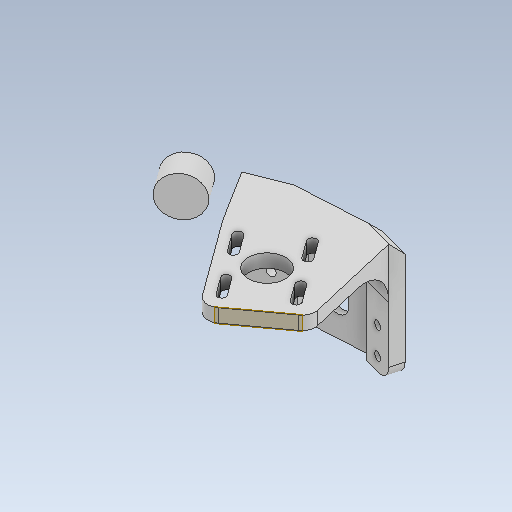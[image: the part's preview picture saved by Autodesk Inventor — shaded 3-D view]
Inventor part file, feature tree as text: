
AUTODESK INVENTOR PART (.ipt)
format: ipt  version: 2020 (Build 240168000, 168)  size: 335,360 bytes
history: native  units: mm
features: reference x10, other x8, sketch x7, extrude x5, fillet x4, projected_geometry x4, plane x2, hole x2, thicken_offset x1, chamfer x1, shell x1
ambient origin geometry x8: Origin, YZ Plane, XZ Plane, XY Plane, X Axis, Y Axis, Z Axis, Center Point
bodies: Solid1 (feature_tree)
feature tree (45):
  plane  "Work Plane1"
  extrude  "Extrusion1"  Depth=5.0mm
  extrude  "Extrusion2"  Depth=5.0mm
  thicken_offset  "Thicken1"
  hole  "Hole1"  [1 undecoded]
  hole  "Hole2"  [1 undecoded]
  extrude  "Extrusion3"  Depth=8.0mm
  fillet  "Fillet1"  Radius=20.0mm
  fillet  "Fillet2"  Radius=20.0mm
  chamfer  "Chamfer1"  Distance=40.0mm
  fillet  "Fillet3"  Radius=4.0mm
  fillet  "Fillet4"  Radius=3.0mm
  extrude  "Extrusion4"  Depth=4.0mm
  plane  "Work Plane2"
  extrude  "Extrusion5"  Depth=10.0mm
  sketch  "Sketch1"  dims[d0=5.0mm d1=5.0mm]
  reference  "Reference1"
  reference  "Reference2"
  reference  "Reference3"
  reference  "Reference4"
  sketch  "Sketch2"  dims[d2=5.0mm d3=5.0mm]
  projected_geometry  "Projected Loop1"
  projected_geometry  "Projected Loop2"
  sketch  "Sketch3"  dims[d4=25.0mm d5=0.0mm d6=25.0mm d7=0.0mm]
  reference  "Reference5"
  reference  "Reference6"
  sketch  "Sketch4"  dims[d8=20.0mm d9=20.0mm]
  reference  "Reference7"
  reference  "Reference8"
  sketch  "Sketch5"  dims[d10=3.0mm d11=6.0mm d12=4.0mm d13=2.0mm d14=90.0deg d15=8.0mm d16=20.594885mm]
  reference  "Reference9"
  projected_geometry  "Projected Loop3"
  sketch  "Sketch6"  dims[d17=3.0mm d18=6.0mm d19=4.0mm d20=2.0mm d21=90.0deg d22=8.0mm d23=20.594885mm d24=102.0mm d25=20.0mm d26=20.0mm]
  projected_geometry  "Projected Loop4"
  sketch  "Sketch7"  dims[d27=30.0mm d28=40.0mm d29=4.0mm d30=3.0mm d31=4.0mm d32=3.2mm d33=4.0mm d34=3.2mm d35=4.0mm d36=3.2mm d37=14.0mm d38=5.0mm d39=0.0mm d40=14.0mm d41=2.0mm d42=5.0mm d43=2.0mm d44=45.0deg d45=5.0mm d46=5.0mm d47=18.0mm d48=6.0mm d49=8.0mm d50=5.0mm d51=0.0mm d52=0.0mm d53=55.0mm d54=15.0mm d55=10.0mm d56=0.0mm]
  reference  "Reference10"
  parser-record x2  (decoder bookkeeping rows leaked as tree rows — omitted from the tree; the rows remain in map.json)
  other  "reducer_2.iam"
  other  "motor_h_1:1"
  shell  "shell_2:1"  Thickness=4.0mm
  other  "t_base_linker_2:1"
  other  "leg_1.iam"
  other  "reducer_2:1"
  other  "bearing_8_16_5:1"
note: 2 required parameter values undecoded (feature->parameter linkage not recoverable at this tier; creation-order binding heuristic only, values carry confidence <= 0.55)
note: 2 file-system paths scrubbed to <path> (originals preserved in map.json)
